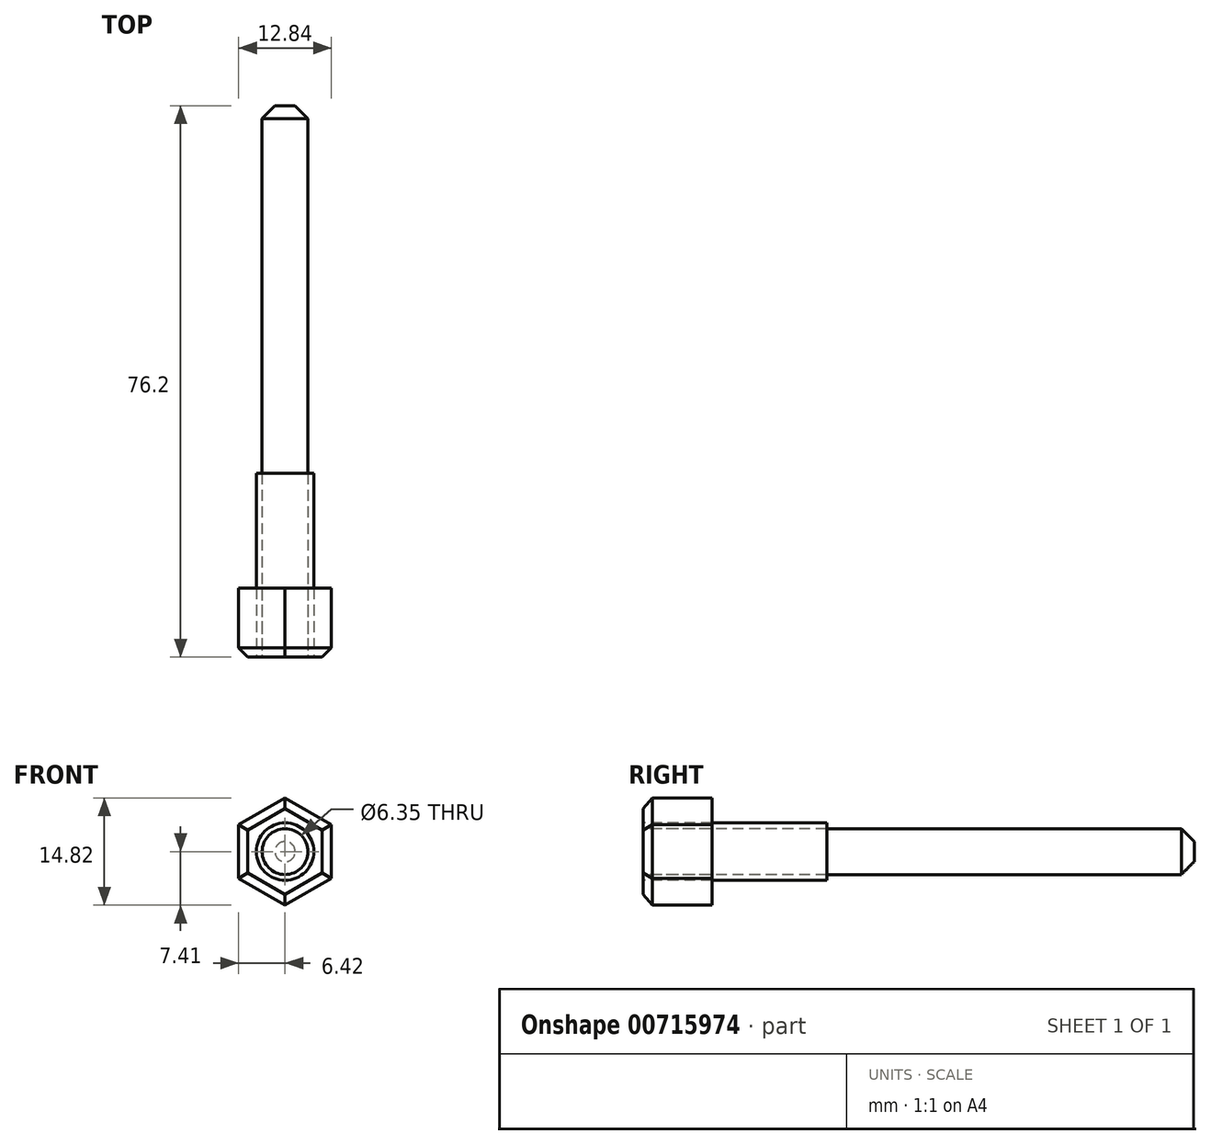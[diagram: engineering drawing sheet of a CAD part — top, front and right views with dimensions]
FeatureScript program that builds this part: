
annotation { "Feature Type Name" : "Feature", "Feature Type Description" : "" }
export const myFeature = defineFeature(function(context is Context, id is Id, definition is map)
    precondition{}
    {
        {
            var Q0;
            Q0=qCreatedBy(makeId("Front.planeOp"),FACE);
            var sketch = newSketch(context, id + "F0", { "sketchPlane" : qUnion([Q0])});
            skCircle(sketch, "E0.cCircle", {"center": v(0, 0) * mm, "radius": 6.42 * mm, "construction": true});
            skLineSegment(sketch, "E0.0", {"start": v(6.42, 3.7) * mm, "end": v(6.42, -3.7) * mm});
            skLineSegment(sketch, "E0.1", {"start": v(6.42, -3.7) * mm, "end": v(0, -7.4) * mm});
            skLineSegment(sketch, "E0.2", {"start": v(0, -7.4) * mm, "end": v(-6.42, -3.7) * mm});
            skLineSegment(sketch, "E0.3", {"start": v(-6.42, -3.7) * mm, "end": v(-6.42, 3.7) * mm});
            skLineSegment(sketch, "E0.4", {"start": v(-6.42, 3.7) * mm, "end": v(0, 7.4) * mm});
            skLineSegment(sketch, "E0.5", {"start": v(0, 7.4) * mm, "end": v(6.42, 3.7) * mm});
            skPoint(sketch, "E0.0.midPoint", {"position": v(6.42, 0) * mm});
            skCircle(sketch, "E1", {"center": v(0, 0) * mm, "radius": 3.18 * mm});
            skSolve(sketch);
        }
        {
            var Q0;
            Q0=makeQuery(id+"F0.imprint","IMPRINT",FACE,{"disambiguationData":[TD([[makeQuery(id+"F0.imprint","IMPRINT",EDGE,{"derivedFrom":sQuery(id+"F0.wireOp",EDGE,"E1")}),1.0]])]});
            extrude(context, id + "F1", {"entities" : qUnion([Q0]), "oppositeDirection" : true, "depth" : 76.2 * mm, "offsetDistance" : 25.4 * mm});
        }
        {
            var Q0;
            Q0=makeQuery(id+"F0.imprint","IMPRINT",FACE,{"disambiguationData":[TD([[makeQuery(id+"F0.imprint","IMPRINT",EDGE,{"derivedFrom":sQuery(id+"F0.wireOp",EDGE,"E0.0")}),-1.0]])]});
            extrude(context, id + "F2", {"entities" : qUnion([Q0]), "oppositeDirection" : true, "depth" : 9.52 * mm, "offsetDistance" : 25.4 * mm});
        }
        {
            var Q0;
            Q0=makeQuery(id+"F2.opExtrude","CAP_EDGE",EDGE,{"disambiguationData":[OSD([sQuery(id+"F0.wireOp",EDGE,"E0.3")])],"isStart":true});
            var Q1;
            Q1=makeQuery(id+"F2.opExtrude","CAP_EDGE",EDGE,{"disambiguationData":[OSD([sQuery(id+"F0.wireOp",EDGE,"E0.2")])],"isStart":true});
            var Q2;
            Q2=makeQuery(id+"F2.opExtrude","CAP_EDGE",EDGE,{"disambiguationData":[OSD([sQuery(id+"F0.wireOp",EDGE,"E0.1")])],"isStart":true});
            var Q3;
            Q3=makeQuery(id+"F2.opExtrude","CAP_EDGE",EDGE,{"disambiguationData":[OSD([sQuery(id+"F0.wireOp",EDGE,"E0.0")])],"isStart":true});
            var Q4;
            Q4=makeQuery(id+"F2.opExtrude","CAP_EDGE",EDGE,{"disambiguationData":[OSD([sQuery(id+"F0.wireOp",EDGE,"E0.5")])],"isStart":true});
            var Q5;
            Q5=makeQuery(id+"F2.opExtrude","CAP_EDGE",EDGE,{"disambiguationData":[OSD([sQuery(id+"F0.wireOp",EDGE,"E0.4")])],"isStart":true});
            chamfer(context, id + "F3", {"entities" : qUnion([Q0, Q1, Q2, Q3, Q4, Q5]), "width" : 1.27 * mm, "tangentPropagation" : true});
        }
        {
            var Q0;
            Q0=qCreatedBy(makeId("Front.planeOp"),FACE);
            var sketch = newSketch(context, id + "F4", { "sketchPlane" : qUnion([Q0])});
            skCircle(sketch, "E2", {"center": v(0, 0) * mm, "radius": 3.97 * mm});
            skSolve(sketch);
        }
        {
            var Q0;
            Q0 = qSketchRegion(id + "F4", true);
            extrude(context, id + "F5", {"entities" : qUnion([Q0]), "oppositeDirection" : true, "depth" : 25.4 * mm, "offsetDistance" : 25.4 * mm});
        }
        {
            var Q0;
            Q0=makeQuery(id+"F1.opExtrude","CAP_EDGE",EDGE,{"disambiguationData":[OSD([sQuery(id+"F0.wireOp",EDGE,"E1")])],"isStart":false});
            chamfer(context, id + "F6", {"entities" : qUnion([Q0]), "width" : 1.78 * mm, "tangentPropagation" : true});
        }
    });
